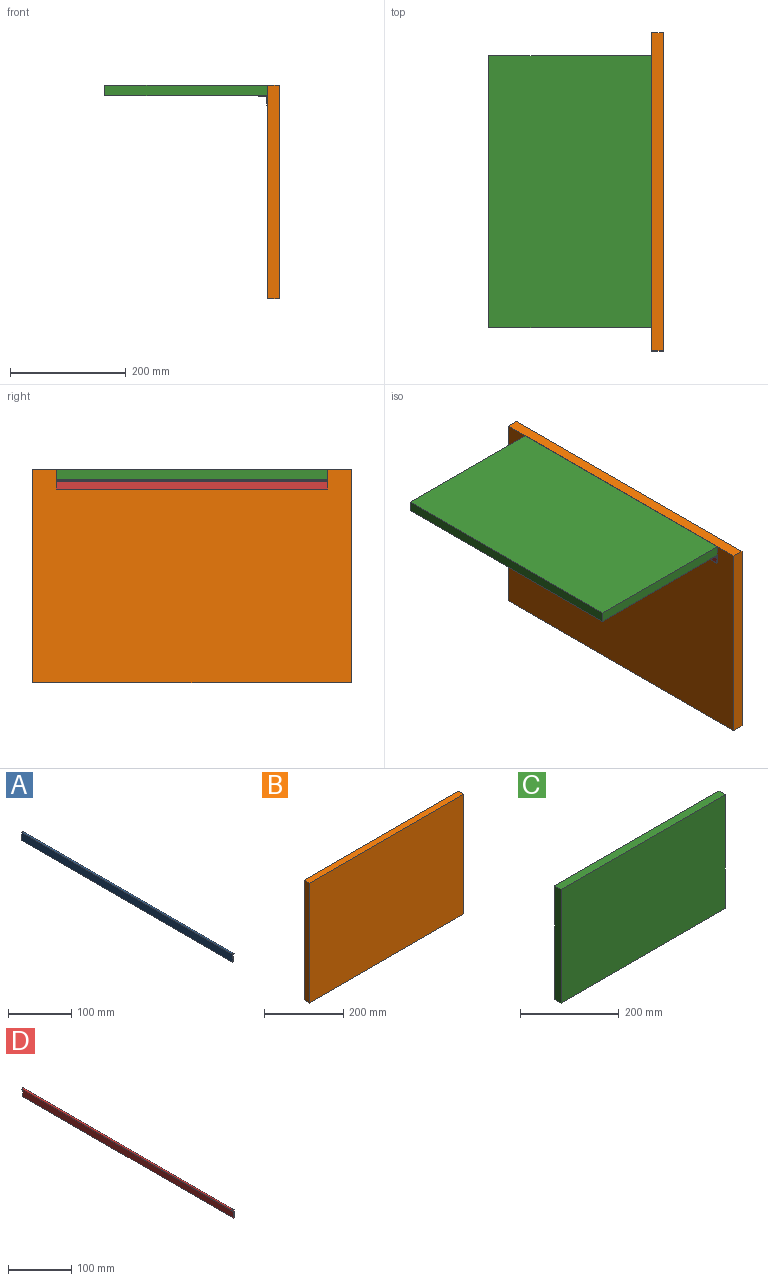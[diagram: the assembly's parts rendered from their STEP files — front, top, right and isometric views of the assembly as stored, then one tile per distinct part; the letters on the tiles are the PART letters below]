
ASSEMBLY  parts=4 mates=3
PART A: 6 faces, bbox 3x470x16.5 mm
  f0: plane 470x13.5mm, normal (1,0,0), area 6345mm2, adj f1,f3,f4,f5
  f1: cylinder r=1.5mm len=470mm, axis (0,1,0), area 3322.2mm2, adj f0,f2,f4,f5
  f2: plane 470x15mm, normal (-1,0,0), area 7050mm2, adj f1,f3,f4,f5
  f3: plane 470x1.5mm, normal (0,0,-1), area 705mm2, adj f0,f2,f4,f5
  f4: plane 16.5x3mm, normal (0,-1,0), area 27.8mm2, adj f0,f1,f2,f3
  f5: plane 16.5x3mm, normal (0,1,0), area 27.8mm2, adj f0,f1,f2,f3
PART B: 6 faces, bbox 550x20x369.5 mm
  f0: plane 369.5x20mm, normal (-1,0,0), area 7390mm2, adj f1,f3,f4,f5
  f1: plane 550x20mm, normal (0,0,-1), area 11000mm2, adj f0,f2,f3,f4
  f2: plane 369.5x20mm, normal (1,0,0), area 7390mm2, adj f1,f3,f4,f5
  f3: plane 550x369.5mm, normal (0,-1,0), area 203225mm2, adj f0,f1,f2,f5
  f4: plane 550x369.5mm, normal (0,1,0), area 203225mm2, adj f0,f1,f2,f5
  f5: plane 550x20mm, normal (0,0,1), area 11000mm2, adj f0,f2,f3,f4
PART C: 6 faces, bbox 470x18x281.5 mm
  f0: plane 281.5x18mm, normal (-1,0,0), area 5067mm2, adj f1,f3,f4,f5
  f1: plane 470x18mm, normal (0,0,-1), area 8460mm2, adj f0,f2,f3,f4
  f2: plane 281.5x18mm, normal (1,0,0), area 5067mm2, adj f1,f3,f4,f5
  f3: plane 470x281.5mm, normal (0,-1,0), area 132305mm2, adj f0,f1,f2,f5
  f4: plane 470x281.5mm, normal (0,1,0), area 132305mm2, adj f0,f1,f2,f5
  f5: plane 470x18mm, normal (0,0,1), area 8460mm2, adj f0,f2,f3,f4
PART D: 6 faces, bbox 3x470x16.5 mm
  f0: cylinder r=1.5mm len=470mm, axis (0,1,0), area 3322.2mm2, adj f1,f3,f4,f5
  f1: plane 470x13.5mm, normal (-1,0,0), area 6345mm2, adj f0,f2,f4,f5
  f2: plane 470x1.5mm, normal (0,0,-1), area 705mm2, adj f1,f3,f4,f5
  f3: plane 470x15mm, normal (1,0,0), area 7050mm2, adj f0,f2,f4,f5
  f4: plane 16.5x3mm, normal (0,-1,0), area 27.8mm2, adj f0,f1,f2,f3
  f5: plane 16.5x3mm, normal (0,1,0), area 27.8mm2, adj f0,f1,f2,f3
PLACE A rot(axis=(0,1,0),90deg) t=(0,0,0)mm
PLACE B rot(axis=(0,0,-1),90deg) t=(21.5,-229.4,-97.52)mm
PLACE C rot(axis=(-0.58,0.58,-0.58),120deg) t=(-50.45,-224.32,1.5)mm
PLACE D at identity fixed
MATE fastened D.f3 <-> B.f3  axis (1,0,0) through (1.5,-235,0)mm
MATE revolute D.f0 <-> A.f1  axis (0,-1,0) through (0,-470,0)mm
MATE fastened A.f2 <-> C.f4  axis (0,0,1) through (0,-235,1.5)mm
